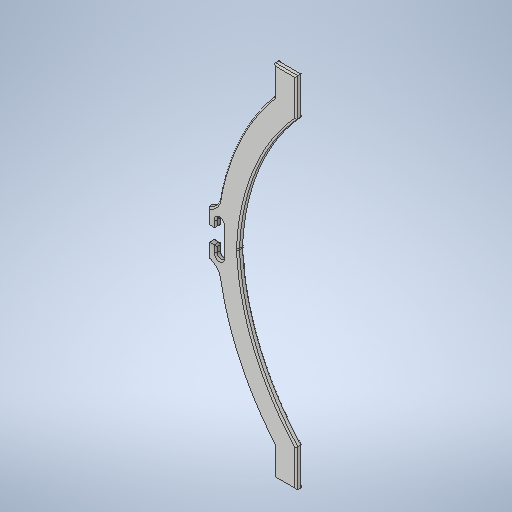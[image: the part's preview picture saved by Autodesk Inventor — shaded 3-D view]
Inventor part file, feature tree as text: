
AUTODESK INVENTOR PART (.ipt)
format: ipt  version: 2025 (Build 290162000, 162)  size: 1,364,480 bytes
history: native  units: mm
features: extrude x3, fillet x2, mirror x1, sketch x1
ambient origin geometry x8: Origin, YZ Plane, XZ Plane, XY Plane, X Axis, Y Axis, Z Axis, Center Point
bodies: Volumenkörper1 (feature_tree)
feature tree (7):
  extrude  "Extrusion1"  Depth=15.0mm
  mirror  "Spiegeln1"
  extrude  "Extrusion2"  Depth=54.0mm
  fillet  "Rundung1"  [1 undecoded]
  fillet  "Rundung2"  Radius=120.0mm
  extrude  "Extrusion3"  Depth=150.0mm
  sketch  "Skizze3"  dims[d0=25.0mm d2=15.0mm d4=54.0mm d5=0.0mm d6=120.0mm d7=150.0mm d9=5.0mm d10=15.0mm d11=15.0mm d12=4.0mm d13=0.0mm d15=10.0mm d16=5.0mm d17=10.0mm d18=5.0mm d19=5.0mm d20=24.0mm d21=4.5mm d22=4.0mm d23=0.0mm d24=10.0mm d25=1.0mm d26=1.0mm d27=0.0mm]
note: 1 required parameter value undecoded (feature->parameter linkage not recoverable at this tier; creation-order binding heuristic only, values carry confidence <= 0.55)
